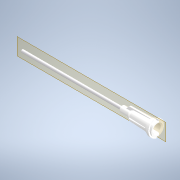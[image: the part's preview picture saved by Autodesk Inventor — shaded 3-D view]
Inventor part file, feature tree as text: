
AUTODESK INVENTOR PART (.ipt)
format: ipt  version: 2021.2 (Build 252289000, 289)  size: 443,392 bytes
history: native  units: in
note: dims shown in document units (in); Inventor stores cm internally (conversion verified against a paired STEP export)
features: other x4, direct_edit x1, plane x1, sketch x1
ambient origin geometry x8: Origin, YZ Plane, XZ Plane, XY Plane, X Axis, Y Axis, Z Axis, Center Point
bodies: Solid1 (feature_tree), Solid2 (feature_tree)
feature tree (7):
  direct_edit  "Direct Edit1"
  plane  "Work Plane1"
  other  "Bend Part1"
  sketch  "Sketch1"  dims[d0=0.9895in d1=0.75in d2=1.2964in d3=0.1057in]
  other  "NeedleBody"
  other  "NeedleShaftExt"
  other  "Size1"
